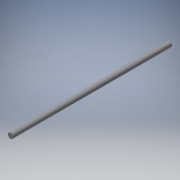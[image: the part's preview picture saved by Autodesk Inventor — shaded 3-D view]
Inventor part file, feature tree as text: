
AUTODESK INVENTOR PART (.ipt)
format: ipt  version: 2019 (Build 230136000, 136)  size: 91,136 bytes
history: native  units: mm
features: extrude x1, sketch x1
ambient origin geometry x8: Origin, YZ Plane, XZ Plane, XY Plane, X Axis, Y Axis, Z Axis, Center Point
bodies: Solid1 (feature_tree)
feature tree (2):
  extrude  "Extrusion1"  Depth=150.0mm TaperAngle=0.0deg
  sketch  "Sketch1"  dims[d0=5.0mm d1=150.0mm d2=0.0mm]
